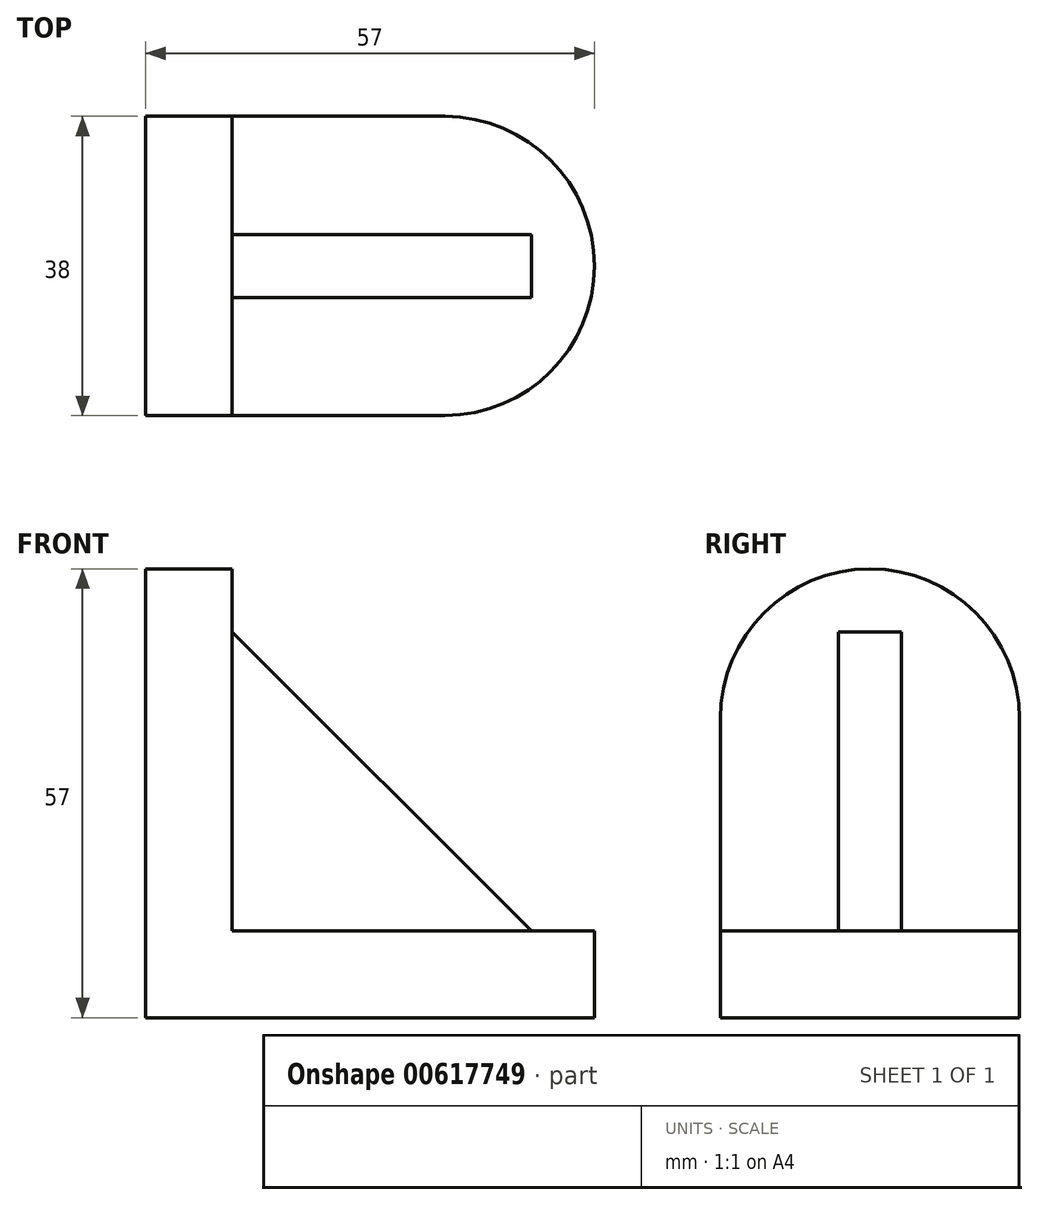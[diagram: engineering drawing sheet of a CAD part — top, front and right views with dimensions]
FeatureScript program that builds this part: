
annotation { "Feature Type Name" : "Feature", "Feature Type Description" : "" }
export const myFeature = defineFeature(function(context is Context, id is Id, definition is map)
    precondition{}
    {
        {
            var Q0;
            Q0=qCreatedBy(makeId("Front.planeOp"),FACE);
            var sketch = newSketch(context, id + "F0", { "sketchPlane" : qUnion([Q0])});
            skLineSegment(sketch, "E0", {"start": v(0, 0) * mm, "end": v(0, 38) * mm});
            skLineSegment(sketch, "E1", {"start": v(0, 38) * mm, "end": v(11, 38) * mm});
            skLineSegment(sketch, "E2", {"start": v(11, 38) * mm, "end": v(11, 11) * mm});
            skLineSegment(sketch, "E3", {"start": v(11, 11) * mm, "end": v(38, 11) * mm});
            skLineSegment(sketch, "E4", {"start": v(38, 11) * mm, "end": v(38, 0) * mm});
            skLineSegment(sketch, "E5", {"start": v(38, 0) * mm, "end": v(0, 0) * mm});
            skSolve(sketch);
        }
        {
            var Q0;
            Q0=makeQuery(id+"F0.imprint","IMPRINT",FACE,{"disambiguationData":[TD([[makeQuery(id+"F0.imprint","IMPRINT",EDGE,{"derivedFrom":sQuery(id+"F0.wireOp",EDGE,"E0")}),-1.0]])]});
            extrude(context, id + "F1", {"entities" : qUnion([Q0]), "depth" : 38 * mm, "offsetDistance" : 25 * mm});
        }
        {
            var Q0;
            Q0=makeQuery(id+"F1.opExtrude","SWEPT_FACE",FACE,{"disambiguationData":[OSD([sQuery(id+"F0.wireOp",EDGE,"E0")])]});
            var sketch = newSketch(context, id + "F2", { "sketchPlane" : qUnion([Q0])});
            skArc(sketch, "E6", {"start": v(38, 38) * mm, "mid": v(19, 57) * mm, "end": v(0, 38) * mm});
            skSolve(sketch);
        }
        {
            var Q0;
            Q0=makeQuery(id+"F2.imprint","IMPRINT",FACE,{"disambiguationData":[TD([[makeQuery(id+"F2.imprint","IMPRINT",EDGE,{"derivedFrom":sQuery(id+"F2.wireOp",EDGE,"E6")}),1.0]])]});
            extrude(context, id + "F3", {"entities" : qUnion([Q0]), "operationType" : NewBodyOperationType.ADD, "oppositeDirection" : true, "depth" : 11 * mm, "offsetDistance" : 25 * mm});
        }
        {
            var Q0;
            Q0=makeQuery(id+"F1.opExtrude","SWEPT_FACE",FACE,{"disambiguationData":[OSD([sQuery(id+"F0.wireOp",EDGE,"E5")])]});
            var sketch = newSketch(context, id + "F4", { "sketchPlane" : qUnion([Q0])});
            skArc(sketch, "E7", {"start": v(38, 0) * mm, "mid": v(57, 19) * mm, "end": v(38, 38) * mm});
            skSolve(sketch);
        }
        {
            var Q0;
            Q0=makeQuery(id+"F4.imprint","IMPRINT",FACE,{"disambiguationData":[TD([[makeQuery(id+"F4.imprint","IMPRINT",EDGE,{"derivedFrom":sQuery(id+"F4.wireOp",EDGE,"E7")}),1.0]])]});
            extrude(context, id + "F5", {"entities" : qUnion([Q0]), "operationType" : NewBodyOperationType.ADD, "oppositeDirection" : true, "depth" : 11 * mm, "offsetDistance" : 25 * mm});
        }
        {
            var Q0;
            Q0=makeQuery(id+"F3.boolean.opBoolean","MERGE",FACE,{"derivedFrom":[makeQuery(id+"F1.opExtrude","SWEPT_FACE",FACE,{"disambiguationData":[OSD([sQuery(id+"F0.wireOp",EDGE,"E2")])]}),makeQuery(id+"F3.opExtrude","CAP_FACE",FACE,{"disambiguationData":[OSD([sQuery(id+"F0.wireOp",EDGE,"E0"),sQuery(id+"F0.wireOp",EDGE,"E1"),sQuery(id+"F2.wireOp",EDGE,"E6")])],"isStart":false})]});
            var sketch = newSketch(context, id + "F6", { "sketchPlane" : qUnion([Q0])});
            skLineSegment(sketch, "E8.bottom", {"start": v(-15, 11) * mm, "end": v(-23, 11) * mm});
            skLineSegment(sketch, "E8.top", {"start": v(-15, 49) * mm, "end": v(-23, 49) * mm});
            skLineSegment(sketch, "E8.left", {"start": v(-15, 11) * mm, "end": v(-15, 49) * mm});
            skLineSegment(sketch, "E8.right", {"start": v(-23, 11) * mm, "end": v(-23, 49) * mm});
            skSolve(sketch);
        }
        {
            var Q0;
            Q0=makeQuery(id+"F6.imprint","IMPRINT",FACE,{"disambiguationData":[TD([[makeQuery(id+"F6.imprint","IMPRINT",EDGE,{"derivedFrom":sQuery(id+"F6.wireOp",EDGE,"E8.bottom")}),1.0]])]});
            extrude(context, id + "F7", {"entities" : qUnion([Q0]), "operationType" : NewBodyOperationType.ADD, "depth" : 38 * mm, "offsetDistance" : 25 * mm});
        }
        {
            var Q0;
            Q0=makeQuery(id+"F7.opExtrude","SWEPT_FACE",FACE,{"disambiguationData":[OSD([sQuery(id+"F6.wireOp",EDGE,"E8.right")])]});
            var sketch = newSketch(context, id + "F8", { "sketchPlane" : qUnion([Q0])});
            skLineSegment(sketch, "E9", {"start": v(11, 11) * mm, "end": v(49, 11) * mm});
            skLineSegment(sketch, "E10", {"start": v(49, 11) * mm, "end": v(11, 49) * mm});
            skLineSegment(sketch, "E11", {"start": v(11, 49) * mm, "end": v(11, 11) * mm});
            skSolve(sketch);
        }
        {
            var Q0;
            Q0=makeQuery(id+"F8.imprint","IMPRINT",FACE,{"disambiguationData":[TD([[makeQuery(id+"F8.imprint","IMPRINT",EDGE,{"derivedFrom":sQuery(id+"F8.wireOp",EDGE,"E10")}),-1.0]])]});
            extrude(context, id + "F9", {"entities" : qUnion([Q0]), "operationType" : NewBodyOperationType.REMOVE, "oppositeDirection" : true, "depth" : 25 * mm, "offsetDistance" : 25 * mm});
        }
    });
